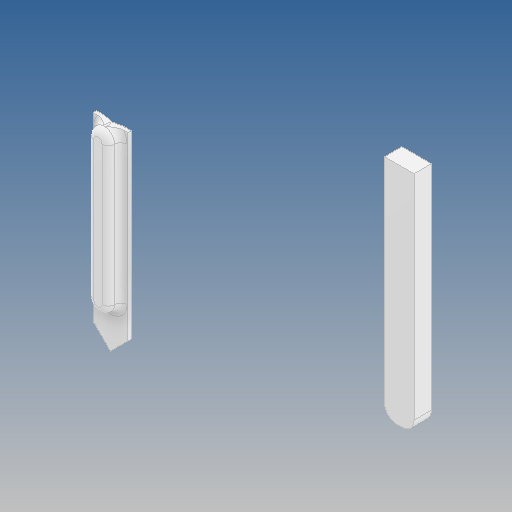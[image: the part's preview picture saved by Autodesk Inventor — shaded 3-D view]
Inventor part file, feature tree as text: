
AUTODESK INVENTOR PART (.ipt)
format: ipt  version: 2020 (Build 240168000, 168)  size: 142,336 bytes
history: native  units: in
note: dims shown in document units (in); Inventor stores cm internally (conversion verified against a paired STEP export)
features: fillet x2
ambient origin geometry x8: Origin, YZ Plane, XZ Plane, XY Plane, X Axis, Y Axis, Z Axis, Center Point
bodies: Solid1 (feature_tree), Solid2 (feature_tree)
feature tree (2):
  fillet  "Fillet1"  [1 undecoded]
  fillet  "Fillet2"  [1 undecoded]
note: 2 required parameter values undecoded (feature->parameter linkage not recoverable at this tier; creation-order binding heuristic only, values carry confidence <= 0.55)
